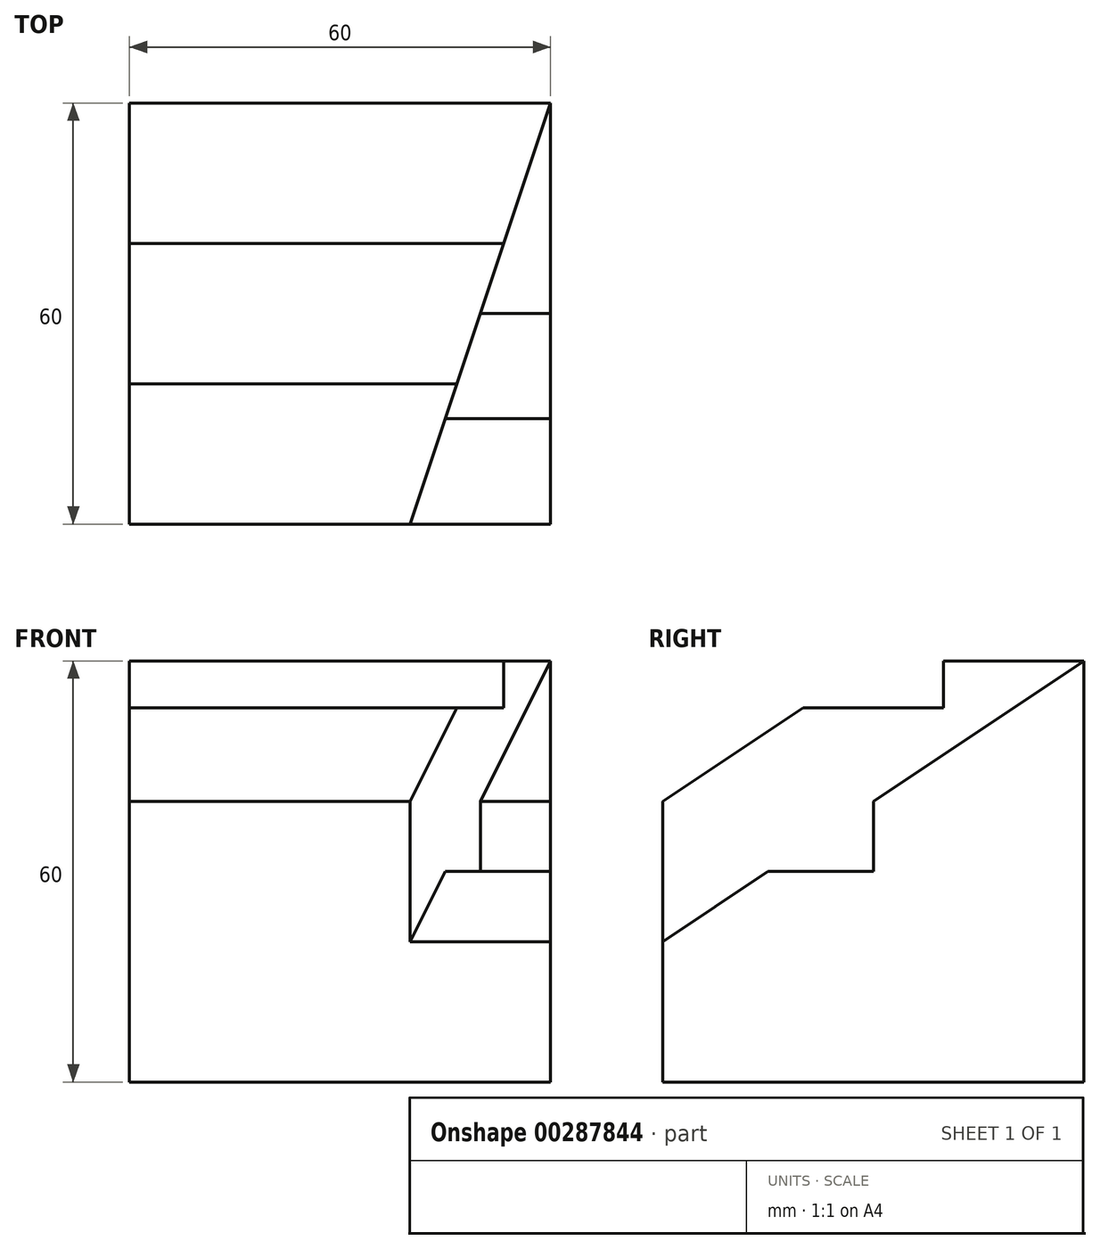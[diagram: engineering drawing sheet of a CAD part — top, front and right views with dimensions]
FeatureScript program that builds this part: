
annotation { "Feature Type Name" : "Feature", "Feature Type Description" : "" }
export const myFeature = defineFeature(function(context is Context, id is Id, definition is map)
    precondition{}
    {
        {
            var Q0;
            Q0=qCreatedBy(makeId("Front.planeOp"),FACE);
            var sketch = newSketch(context, id + "F0", { "sketchPlane" : qUnion([Q0])});
            skLineSegment(sketch, "E0.bottom", {"start": v(0, 0) * mm, "end": v(60, 0) * mm});
            skLineSegment(sketch, "E0.top", {"start": v(0, 60) * mm, "end": v(60, 60) * mm});
            skLineSegment(sketch, "E0.left", {"start": v(0, 0) * mm, "end": v(0, 60) * mm});
            skLineSegment(sketch, "E0.right", {"start": v(60, 0) * mm, "end": v(60, 60) * mm});
            skSolve(sketch);
        }
        {
            var Q0;
            Q0=makeQuery(id+"F0.imprint","IMPRINT",FACE,{"disambiguationData":[TD([[makeQuery(id+"F0.imprint","IMPRINT",EDGE,{"derivedFrom":sQuery(id+"F0.wireOp",EDGE,"E0.bottom")}),1.0]])]});
            extrude(context, id + "F1", {"entities" : qUnion([Q0]), "depth" : 60 * mm});
        }
        {
            var Q0;
            Q0=makeQuery(id+"F1.opExtrude","SWEPT_FACE",FACE,{"disambiguationData":[OSD([sQuery(id+"F0.wireOp",EDGE,"E0.right")])]});
            var sketch = newSketch(context, id + "F2", { "sketchPlane" : qUnion([Q0])});
            skLineSegment(sketch, "E1", {"start": v(-40, 53.33) * mm, "end": v(-60, 40) * mm});
            skLineSegment(sketch, "E2", {"start": v(-40, 53.33) * mm, "end": v(-20, 53.33) * mm});
            skLineSegment(sketch, "E3", {"start": v(-20, 53.33) * mm, "end": v(-20, 60) * mm});
            skPoint(sketch, "E4.orphan", {"position": v(-30, 60) * mm});
            skLineSegment(sketch, "E5", {"start": v(-20, 60) * mm, "end": v(-60, 60) * mm});
            skLineSegment(sketch, "E6", {"start": v(-60, 60) * mm, "end": v(-60, 40) * mm});
            skSolve(sketch);
        }
        {
            var Q0;
            Q0 = qSketchRegion(id + "F2", true);
            extrude(context, id + "F3", {"entities" : qUnion([Q0]), "operationType" : NewBodyOperationType.REMOVE, "endBound" : BoundingType.THROUGH_ALL, "oppositeDirection" : true, "depth" : 25 * mm});
        }
        {
            var Q0;
            Q0=makeQuery(id+"F1.opExtrude","CAP_FACE",FACE,{"disambiguationData":[OSD([sQuery(id+"F0.wireOp",EDGE,"E0.bottom"),sQuery(id+"F0.wireOp",EDGE,"E0.top"),sQuery(id+"F0.wireOp",EDGE,"E0.left"),sQuery(id+"F0.wireOp",EDGE,"E0.right")])],"isStart":false});
            var sketch = newSketch(context, id + "F4", { "sketchPlane" : qUnion([Q0])});
            skLineSegment(sketch, "E7", {"start": v(0, 20) * mm, "end": v(20, 20) * mm});
            skLineSegment(sketch, "E8", {"start": v(20, 20) * mm, "end": v(20, 40) * mm});
            skLineSegment(sketch, "E9", {"start": v(20, 40) * mm, "end": v(40, 40) * mm});
            skLineSegment(sketch, "E10", {"start": v(40, 40) * mm, "end": v(40, 20) * mm});
            skLineSegment(sketch, "E11", {"start": v(40, 20) * mm, "end": v(60, 20) * mm});
            skSolve(sketch);
        }
        {
            var Q0;
            Q0=makeQuery(id+"F1.opExtrude","CAP_VERTEX",VERTEX,{"disambiguationData":[OSD([sQuery(id+"F0.wireOp",EDGE,"E0.top"),sQuery(id+"F0.wireOp",EDGE,"E0.right")])],"isStart":true});
            var Q1;
            Q1=sQuery(id+"F4.wireOp",VERTEX,"E10.start");
            var Q2;
            Q2=sQuery(id+"F4.wireOp",VERTEX,"E11.start");
            cPlane(context, id + "F5", {"entities" : qUnion([Q0, Q1, Q2]), "cplaneType" : CPlaneType.THREE_POINT, "offset" : 25 * mm, "width" : 150 * mm, "height" : 150 * mm});
        }
        {
            var Q0;
            Q0=qCreatedBy(id+"F5.planeOp",FACE);
            var sketch = newSketch(context, id + "F6", { "sketchPlane" : qUnion([Q0])});
            skLineSegment(sketch, "E12", {"start": v(44.27, 40) * mm, "end": v(23.2, 53.33) * mm});
            skLineSegment(sketch, "E13", {"start": v(44.27, 20) * mm, "end": v(44.27, 40) * mm});
            skLineSegment(sketch, "E14", {"start": v(-18.97, 0) * mm, "end": v(-18.97, 60) * mm});
            skLineSegment(sketch, "E15", {"start": v(2.1, 53.33) * mm, "end": v(23.2, 53.33) * mm});
            skLineSegment(sketch, "E16", {"start": v(2.1, 60) * mm, "end": v(2.1, 53.33) * mm});
            skLineSegment(sketch, "E17", {"start": v(2.1, 60) * mm, "end": v(-18.97, 60) * mm});
            skLineSegment(sketch, "E18", {"start": v(44.27, 20) * mm, "end": v(-18.97, 60) * mm});
            skSolve(sketch);
        }
        {
            var Q0;
            Q0 = qSketchRegion(id + "F6", true);
            extrude(context, id + "F7", {"entities" : qUnion([Q0]), "operationType" : NewBodyOperationType.REMOVE, "endBound" : BoundingType.THROUGH_ALL, "oppositeDirection" : true, "depth" : 25 * mm});
        }
        {
            var Q0;
            Q0=makeQuery(id+"F1.opExtrude","SWEPT_FACE",FACE,{"disambiguationData":[OSD([sQuery(id+"F0.wireOp",EDGE,"E0.right")])]});
            var sketch = newSketch(context, id + "F8", { "sketchPlane" : qUnion([Q0])});
            skLineSegment(sketch, "E19.0", {"start": v(-60, 24) * mm, "end": v(0, 60) * mm});
            skLineSegment(sketch, "E20.0", {"start": v(-60, 24) * mm, "end": v(-60, 20) * mm});
            skLineSegment(sketch, "E21", {"start": v(-60, 20) * mm, "end": v(0, 60) * mm});
            skSolve(sketch);
        }
        {
            var Q0;
            Q0 = qSketchRegion(id + "F8", true);
            var Q1;
            Q1=makeQuery(id+"F7.boolean.opBoolean","COPY",FACE,{"derivedFrom":makeQuery(id+"F7.opExtrude","CAP_FACE",FACE,{"disambiguationData":[OSD([sQuery(id+"F6.wireOp",EDGE,"E13"),sQuery(id+"F6.wireOp",EDGE,"E12"),sQuery(id+"F6.wireOp",EDGE,"E15"),sQuery(id+"F6.wireOp",EDGE,"E16"),sQuery(id+"F6.wireOp",EDGE,"E17"),sQuery(id+"F6.wireOp",EDGE,"E18")])],"isStart":true})});
            extrude(context, id + "F9", {"entities" : qUnion([Q0]), "operationType" : NewBodyOperationType.REMOVE, "endBound" : BoundingType.UP_TO_SURFACE, "oppositeDirection" : true, "endBoundEntityFace" : qUnion([Q1]), "depth" : 25 * mm});
        }
        {
            var Q0;
            Q0=makeQuery(id+"F1.opExtrude","SWEPT_FACE",FACE,{"disambiguationData":[OSD([sQuery(id+"F0.wireOp",EDGE,"E0.left")])]});
            cPlane(context, id + "F10", {"entities" : qUnion([Q0]), "cplaneType" : CPlaneType.OFFSET, "offset" : 30 * mm, "oppositeDirection" : true, "width" : 150 * mm, "height" : 150 * mm});
        }
        {
            var Q0;
            Q0=makeQuery(id+"F1.opExtrude","SWEPT_FACE",FACE,{"disambiguationData":[OSD([sQuery(id+"F0.wireOp",EDGE,"E0.right")])]});
            var sketch = newSketch(context, id + "F11", { "sketchPlane" : qUnion([Q0])});
            skLineSegment(sketch, "E22", {"start": v(-30, 40) * mm, "end": v(-30, 30) * mm});
            skLineSegment(sketch, "E23", {"start": v(-30, 30) * mm, "end": v(-45, 30) * mm});
            skSolve(sketch);
        }
        {
            var Q0;
            {var subQ0=sQuery(id+"F11.wireOp",EDGE,"E22");Q0=makeQuery(id+"F11.imprint","IMPRINT",FACE,{"disambiguationData":[TD([[makeQuery(id+"F11.imprint","IMPRINT",EDGE,{"derivedFrom":subQ0}),-1.0]])]});}
            var Q1;
            Q1=makeQuery(id+"F7.boolean.opBoolean","COPY",FACE,{"derivedFrom":makeQuery(id+"F7.opExtrude","CAP_FACE",FACE,{"disambiguationData":[OSD([sQuery(id+"F6.wireOp",EDGE,"E13"),sQuery(id+"F6.wireOp",EDGE,"E12"),sQuery(id+"F6.wireOp",EDGE,"E15"),sQuery(id+"F6.wireOp",EDGE,"E16"),sQuery(id+"F6.wireOp",EDGE,"E17"),sQuery(id+"F6.wireOp",EDGE,"E18")])],"isStart":true})});
            extrude(context, id + "F12", {"entities" : qUnion([Q0]), "operationType" : NewBodyOperationType.REMOVE, "endBound" : BoundingType.UP_TO_SURFACE, "oppositeDirection" : true, "endBoundEntityFace" : qUnion([Q1]), "depth" : 25 * mm});
        }
    });
